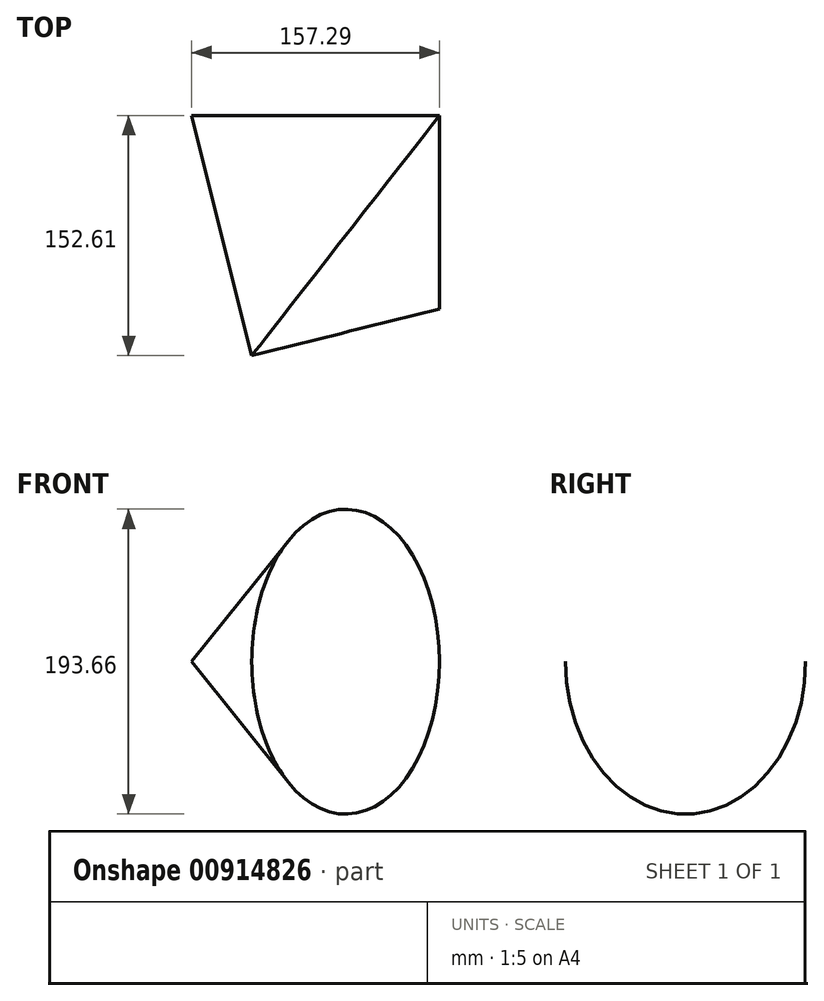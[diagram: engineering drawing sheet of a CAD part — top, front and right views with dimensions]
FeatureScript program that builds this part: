
annotation { "Feature Type Name" : "Feature", "Feature Type Description" : "" }
export const myFeature = defineFeature(function(context is Context, id is Id, definition is map)
    precondition{}
    {
        {
            var Q0;
            Q0=qCreatedBy(makeId("Top.planeOp"),FACE);
            var sketch = newSketch(context, id + "F0", { "sketchPlane" : qUnion([Q0])});
            skLineSegment(sketch, "E0", {"start": v(0, 0) * mm, "end": v(-102.98, 0) * mm, "construction": true});
            skLineSegment(sketch, "E1", {"start": v(0, 0) * mm, "end": v(-157.29, 122.87) * mm});
            skLineSegment(sketch, "E2", {"start": v(-157.29, 122.87) * mm, "end": v(0, 122.87) * mm});
            skLineSegment(sketch, "E3", {"start": v(0, 122.87) * mm, "end": v(0, 0) * mm});
            skSolve(sketch);
        }
        {
            var Q0;
            Q0 = qSketchRegion(id + "F0", true);
            var Q1;
            Q1=sQuery(id+"F0.wireOp",EDGE,"E1");
            revolve(context, id + "F1", {"surfaceOperationType" : NewSurfaceOperationType.NEW, "entities" : qUnion([Q0]), "axis" : qUnion([Q1]), "revolveType" : RevolveType.FULL});
        }
    });
